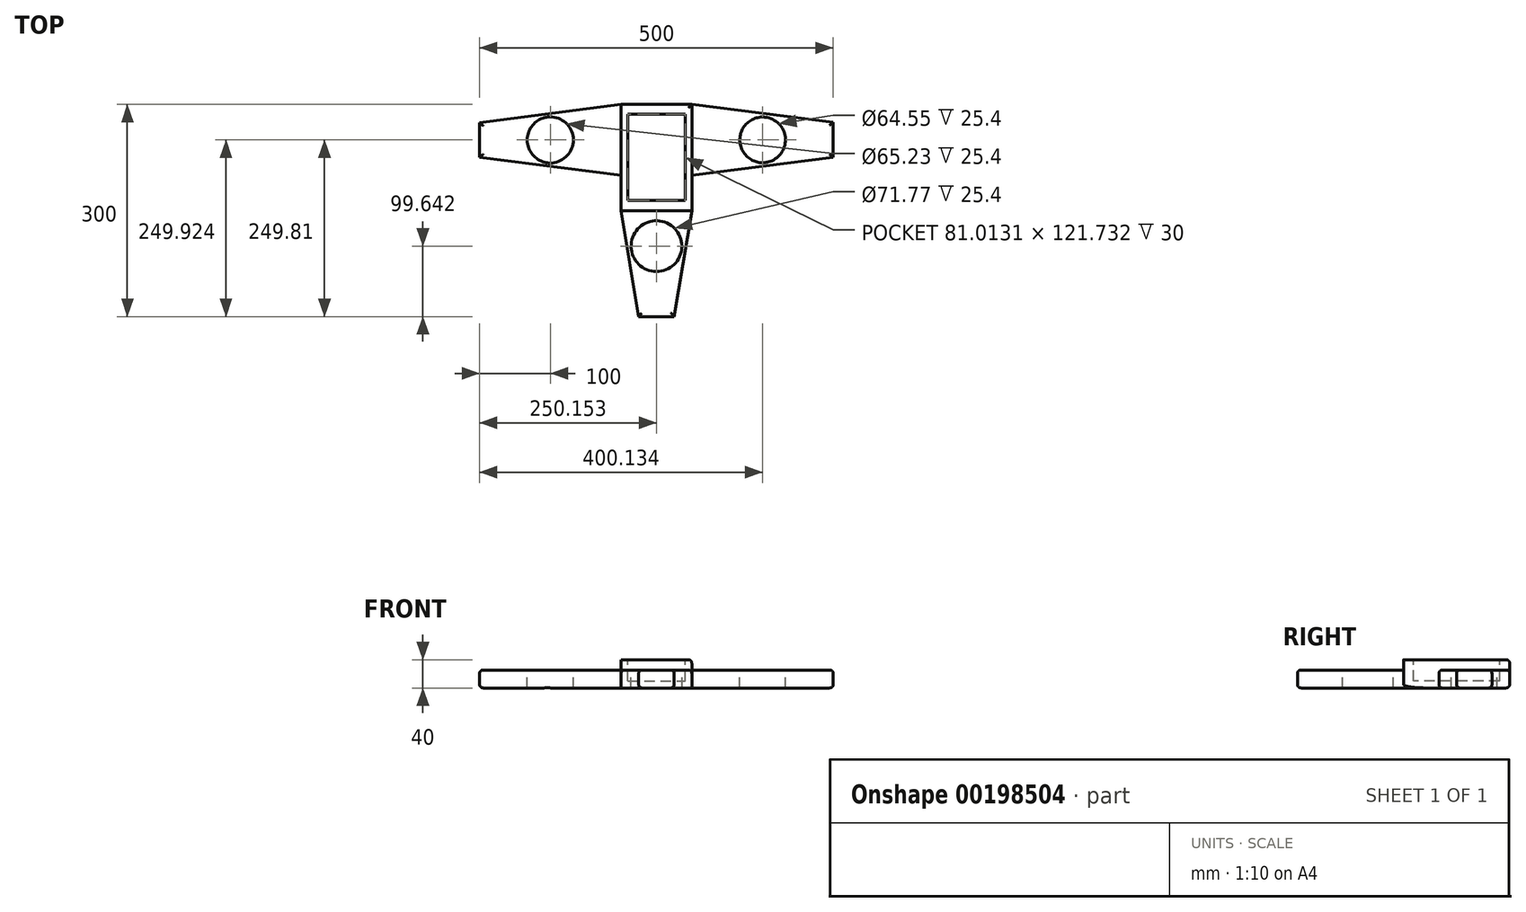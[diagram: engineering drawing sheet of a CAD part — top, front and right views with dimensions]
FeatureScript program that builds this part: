
annotation { "Feature Type Name" : "Feature", "Feature Type Description" : "" }
export const myFeature = defineFeature(function(context is Context, id is Id, definition is map)
    precondition{}
    {
        {
            var Q0;
            Q0=qCreatedBy(makeId("Top.planeOp"),FACE);
            var sketch = newSketch(context, id + "F0", { "sketchPlane" : qUnion([Q0])});
            skLineSegment(sketch, "E0.bottom", {"start": v(50, 50) * mm, "end": v(-50, 50) * mm});
            skLineSegment(sketch, "E0.top", {"start": v(50, -50) * mm, "end": v(-50, -50) * mm});
            skLineSegment(sketch, "E0.left", {"start": v(50, 50) * mm, "end": v(50, -50) * mm});
            skLineSegment(sketch, "E0.right", {"start": v(-50, 50) * mm, "end": v(-50, -50) * mm});
            skPoint(sketch, "E0.middle", {"position": v(0, 0) * mm});
            skLineSegment(sketch, "E1", {"start": v(-50, 25) * mm, "end": v(50, 25) * mm, "construction": true});
            skLineSegment(sketch, "E2", {"start": v(-50, -25) * mm, "end": v(50, -25) * mm, "construction": true});
            skLineSegment(sketch, "E3", {"start": v(-250, 24.24) * mm, "end": v(-45.96, 25) * mm, "construction": true});
            skLineSegment(sketch, "E4", {"start": v(-50, -25) * mm, "end": v(-250, -25) * mm, "construction": true});
            skLineSegment(sketch, "E5", {"start": v(50, 25) * mm, "end": v(250, 25) * mm, "construction": true});
            skLineSegment(sketch, "E6", {"start": v(50, -25) * mm, "end": v(250, -25) * mm, "construction": true});
            skLineSegment(sketch, "E7", {"start": v(-250, 24.24) * mm, "end": v(-50, 50) * mm});
            skLineSegment(sketch, "E8", {"start": v(-250, -25) * mm, "end": v(-50, -50) * mm});
            skLineSegment(sketch, "E9", {"start": v(-250, 24.24) * mm, "end": v(-250, -25) * mm});
            skLineSegment(sketch, "E10", {"start": v(50, 50) * mm, "end": v(250, 25) * mm});
            skLineSegment(sketch, "E11", {"start": v(50, -50) * mm, "end": v(250, -25) * mm});
            skLineSegment(sketch, "E12", {"start": v(250, 25) * mm, "end": v(250, -25) * mm});
            skLineSegment(sketch, "E13", {"start": v(-50, -50) * mm, "end": v(-50, -100) * mm});
            skLineSegment(sketch, "E14", {"start": v(-50, -100) * mm, "end": v(50, -100) * mm});
            skLineSegment(sketch, "E15", {"start": v(50, -100) * mm, "end": v(50, -50) * mm});
            skLineSegment(sketch, "E16", {"start": v(-25, -50) * mm, "end": v(-25, -100) * mm, "construction": true});
            skLineSegment(sketch, "E17", {"start": v(-25, -100) * mm, "end": v(25, -50) * mm, "construction": true});
            skLineSegment(sketch, "E18", {"start": v(25, -50) * mm, "end": v(25, -100) * mm, "construction": true});
            skLineSegment(sketch, "E19", {"start": v(-25, -100) * mm, "end": v(-25, -250) * mm, "construction": true});
            skLineSegment(sketch, "E20", {"start": v(25, -100) * mm, "end": v(25, -250) * mm, "construction": true});
            skLineSegment(sketch, "E21", {"start": v(-50, -100) * mm, "end": v(-25, -250) * mm});
            skLineSegment(sketch, "E22", {"start": v(25, -250) * mm, "end": v(50, -100) * mm});
            skLineSegment(sketch, "E23", {"start": v(-25, -250) * mm, "end": v(25, -250) * mm});
            skSolve(sketch);
        }
        {
            var Q0;
            Q0=makeQuery(id+"F0.imprint","IMPRINT",FACE,{"disambiguationData":[TD([[makeQuery(id+"F0.imprint","IMPRINT",EDGE,{"derivedFrom":sQuery(id+"F0.wireOp",EDGE,"E0.bottom")}),1.0]])]});
            extrude(context, id + "F1", {"entities" : qUnion([Q0]), "depth" : 40 * mm});
        }
        {
            var Q0;
            Q0=makeQuery(id+"F0.imprint","IMPRINT",FACE,{"disambiguationData":[TD([[makeQuery(id+"F0.imprint","IMPRINT",EDGE,{"derivedFrom":sQuery(id+"F0.wireOp",EDGE,"E0.left")}),1.0]])]});
            extrude(context, id + "F2", {"entities" : qUnion([Q0]), "operationType" : NewBodyOperationType.ADD, "depth" : 10 * mm});
        }
        {
            var Q0;
            Q0=makeQuery(id+"F0.imprint","IMPRINT",FACE,{"disambiguationData":[TD([[makeQuery(id+"F0.imprint","IMPRINT",EDGE,{"derivedFrom":sQuery(id+"F0.wireOp",EDGE,"E0.right")}),-1.0]])]});
            extrude(context, id + "F3", {"entities" : qUnion([Q0]), "operationType" : NewBodyOperationType.ADD, "depth" : 10 * mm});
        }
        {
            var Q0;
            Q0 = qSketchRegion(id + "F0", true);
            extrude(context, id + "F4", {"entities" : qUnion([Q0]), "operationType" : NewBodyOperationType.ADD, "depth" : 25.4 * mm});
        }
        {
            var Q0;
            Q0=makeQuery(id+"F0.imprint","IMPRINT",FACE,{"disambiguationData":[TD([[makeQuery(id+"F0.imprint","IMPRINT",EDGE,{"derivedFrom":sQuery(id+"F0.wireOp",EDGE,"E0.top")}),1.0]])]});
            extrude(context, id + "F5", {"entities" : qUnion([Q0]), "operationType" : NewBodyOperationType.ADD, "depth" : 40 * mm});
        }
        {
            var Q0;
            {var subQ0=sQuery(id+"F0.wireOp",EDGE,"E7");var subQ1=sQuery(id+"F0.wireOp",EDGE,"E13");var subQ2=sQuery(id+"F0.wireOp",EDGE,"E9");var subQ3=sQuery(id+"F0.wireOp",EDGE,"E8");var subQ4=sQuery(id+"F0.wireOp",EDGE,"E0.bottom");var subQ5=makeQuery(id+"F4.opExtrude","CAP_FACE",FACE,{"disambiguationData":[OSD([subQ4,subQ0,subQ3,subQ2,sQuery(id+"F0.wireOp",EDGE,"E10"),sQuery(id+"F0.wireOp",EDGE,"E11"),sQuery(id+"F0.wireOp",EDGE,"E12"),subQ1,sQuery(id+"F0.wireOp",EDGE,"E15"),sQuery(id+"F0.wireOp",EDGE,"E21"),sQuery(id+"F0.wireOp",EDGE,"E22"),sQuery(id+"F0.wireOp",EDGE,"E23")])],"isStart":false});Q0=makeQuery(id+"F4.boolean.opBoolean","SPLIT",FACE,{"disambiguationData":[TD([makeQuery(id+"F3.opExtrude","SWEPT_FACE",FACE,{"disambiguationData":[OSD([subQ0])]})])],"derivedFrom":subQ5});}
            var sketch = newSketch(context, id + "F6", { "sketchPlane" : qUnion([Q0])});
            skLineSegment(sketch, "E24", {"start": v(-250, -0.38) * mm, "end": v(250.13, 0) * mm, "construction": true});
            skLineSegment(sketch, "E25", {"start": v(0, 50.76) * mm, "end": v(0.23, -250.36) * mm, "construction": true});
            skLineSegment(sketch, "E26", {"start": v(-150, 37.12) * mm, "end": v(-150, -37.5) * mm, "construction": true});
            skLineSegment(sketch, "E27", {"start": v(150.1, 38.78) * mm, "end": v(150.17, -41) * mm, "construction": true});
            skLineSegment(sketch, "E28", {"start": v(-39.6, -150.39) * mm, "end": v(25.4, -150.34) * mm, "construction": true});
            skCircle(sketch, "E29", {"center": v(-150, -0.19) * mm, "radius": 32.61 * mm});
            skCircle(sketch, "E30", {"center": v(150.13, -0.08) * mm, "radius": 32.27 * mm});
            skCircle(sketch, "E31", {"center": v(0.15, -150.36) * mm, "radius": 35.89 * mm});
            skSolve(sketch);
        }
        {
            var Q0;
            Q0=makeQuery(id+"F6.imprint","IMPRINT",FACE,{"disambiguationData":[TD([[makeQuery(id+"F6.imprint","IMPRINT",EDGE,{"derivedFrom":sQuery(id+"F6.wireOp",EDGE,"E29")}),1.0]])]});
            var Q1;
            Q1=makeQuery(id+"F6.imprint","IMPRINT",FACE,{"disambiguationData":[TD([[makeQuery(id+"F6.imprint","IMPRINT",EDGE,{"derivedFrom":sQuery(id+"F6.wireOp",EDGE,"E31")}),1.0]])]});
            var Q2;
            Q2=makeQuery(id+"F6.imprint","IMPRINT",FACE,{"disambiguationData":[TD([[makeQuery(id+"F6.imprint","IMPRINT",EDGE,{"derivedFrom":sQuery(id+"F6.wireOp",EDGE,"E30")}),1.0]])]});
            extrude(context, id + "F7", {"entities" : qUnion([Q0, Q1, Q2]), "operationType" : NewBodyOperationType.REMOVE, "oppositeDirection" : true, "depth" : 51.3 * mm});
        }
        {
            var Q0;
            {var subQ0=sQuery(id+"F0.wireOp",EDGE,"E0.top");Q0=makeQuery(id+"F5.boolean.opBoolean","MERGE",FACE,{"derivedFrom":[makeQuery(id+"F1.opExtrude","CAP_FACE",FACE,{"disambiguationData":[OSD([sQuery(id+"F0.wireOp",EDGE,"E0.bottom"),subQ0,sQuery(id+"F0.wireOp",EDGE,"E0.left"),sQuery(id+"F0.wireOp",EDGE,"E0.right")])],"isStart":false}),makeQuery(id+"F5.opExtrude","CAP_FACE",FACE,{"disambiguationData":[OSD([subQ0,sQuery(id+"F0.wireOp",EDGE,"E13"),sQuery(id+"F0.wireOp",EDGE,"E14"),sQuery(id+"F0.wireOp",EDGE,"E15")])],"isStart":false})]});}
            var sketch = newSketch(context, id + "F8", { "sketchPlane" : qUnion([Q0])});
            skLineSegment(sketch, "E32", {"start": v(-50, 40) * mm, "end": v(50, 40) * mm, "construction": true});
            skLineSegment(sketch, "E33", {"start": v(40, 50) * mm, "end": v(40, -100) * mm, "construction": true});
            skLineSegment(sketch, "E34", {"start": v(-40, 50) * mm, "end": v(-40, -100) * mm, "construction": true});
            skLineSegment(sketch, "E35", {"start": v(-50, -90) * mm, "end": v(50, -90) * mm, "construction": true});
            skLineSegment(sketch, "E36", {"start": v(-40, 40) * mm, "end": v(40, 40) * mm});
            skLineSegment(sketch, "E37", {"start": v(40, 40) * mm, "end": v(40, -90) * mm});
            skLineSegment(sketch, "E38", {"start": v(40, -90) * mm, "end": v(-40, -90) * mm});
            skLineSegment(sketch, "E39", {"start": v(-40, -90) * mm, "end": v(-40, 40) * mm});
            skSolve(sketch);
        }
        {
            var Q0;
            Q0=makeQuery(id+"F8.imprint","IMPRINT",FACE,{"disambiguationData":[TD([[makeQuery(id+"F8.imprint","IMPRINT",EDGE,{"derivedFrom":sQuery(id+"F8.wireOp",EDGE,"E36")}),-1.0]])]});
            extrude(context, id + "F9", {"entities" : qUnion([Q0]), "operationType" : NewBodyOperationType.ADD, "oppositeDirection" : true, "depth" : 40 * mm});
        }
        {
            var Q0;
            {var subQ0=sQuery(id+"F0.wireOp",EDGE,"E0.top");Q0=makeQuery(id+"F5.boolean.opBoolean","MERGE",FACE,{"derivedFrom":[makeQuery(id+"F1.opExtrude","CAP_FACE",FACE,{"disambiguationData":[OSD([sQuery(id+"F0.wireOp",EDGE,"E0.bottom"),subQ0,sQuery(id+"F0.wireOp",EDGE,"E0.left"),sQuery(id+"F0.wireOp",EDGE,"E0.right")])],"isStart":false}),makeQuery(id+"F5.opExtrude","CAP_FACE",FACE,{"disambiguationData":[OSD([subQ0,sQuery(id+"F0.wireOp",EDGE,"E13"),sQuery(id+"F0.wireOp",EDGE,"E14"),sQuery(id+"F0.wireOp",EDGE,"E15")])],"isStart":false})]});}
            var sketch = newSketch(context, id + "F10", { "sketchPlane" : qUnion([Q0])});
            skLineSegment(sketch, "E40.bottom", {"start": v(-40.22, 36.05) * mm, "end": v(40.8, 36.05) * mm});
            skLineSegment(sketch, "E40.top", {"start": v(-40.22, -85.68) * mm, "end": v(40.8, -85.68) * mm});
            skLineSegment(sketch, "E40.left", {"start": v(-40.22, 36.05) * mm, "end": v(-40.22, -85.68) * mm});
            skLineSegment(sketch, "E40.right", {"start": v(40.8, 36.05) * mm, "end": v(40.8, -85.68) * mm});
            skSolve(sketch);
        }
        {
            var Q0;
            Q0=makeQuery(id+"F10.imprint","IMPRINT",FACE,{"disambiguationData":[TD([[makeQuery(id+"F10.imprint","IMPRINT",EDGE,{"derivedFrom":sQuery(id+"F10.wireOp",EDGE,"E40.bottom")}),-1.0]])]});
            extrude(context, id + "F11", {"entities" : qUnion([Q0]), "operationType" : NewBodyOperationType.REMOVE, "oppositeDirection" : true, "depth" : 30 * mm});
        }
        {
            var Q0;
            Q0=makeQuery(id+"F4.opExtrude","CAP_EDGE",EDGE,{"disambiguationData":[OSD([sQuery(id+"F0.wireOp",EDGE,"E10")])],"isStart":false});
            var Q1;
            Q1=makeQuery(id+"F4.opExtrude","CAP_EDGE",EDGE,{"disambiguationData":[OSD([sQuery(id+"F0.wireOp",EDGE,"E12")])],"isStart":false});
            var Q2;
            Q2=makeQuery(id+"F4.opExtrude","CAP_EDGE",EDGE,{"disambiguationData":[OSD([sQuery(id+"F0.wireOp",EDGE,"E11")])],"isStart":false});
            var Q3;
            Q3=makeQuery(id+"F5.boolean.opBoolean","MERGE",EDGE,{"derivedFrom":[makeQuery(id+"F1.opExtrude","CAP_EDGE",EDGE,{"disambiguationData":[OSD([sQuery(id+"F0.wireOp",EDGE,"E0.left")])],"isStart":false}),makeQuery(id+"F5.opExtrude","CAP_EDGE",EDGE,{"disambiguationData":[OSD([sQuery(id+"F0.wireOp",EDGE,"E15")])],"isStart":false})]});
            var Q4;
            Q4=makeQuery(id+"F11.boolean.opBoolean","COPY",EDGE,{"derivedFrom":makeQuery(id+"F11.opExtrude","CAP_EDGE",EDGE,{"disambiguationData":[OSD([sQuery(id+"F10.wireOp",EDGE,"E40.right")])],"isStart":true})});
            var Q5;
            Q5=makeQuery(id+"F11.boolean.opBoolean","COPY",EDGE,{"derivedFrom":makeQuery(id+"F11.opExtrude","CAP_EDGE",EDGE,{"disambiguationData":[OSD([sQuery(id+"F10.wireOp",EDGE,"E40.bottom")])],"isStart":true})});
            var Q6;
            Q6=makeQuery(id+"F11.boolean.opBoolean","COPY",EDGE,{"derivedFrom":makeQuery(id+"F11.opExtrude","CAP_EDGE",EDGE,{"disambiguationData":[OSD([sQuery(id+"F10.wireOp",EDGE,"E40.left")])],"isStart":true})});
            var Q7;
            Q7=makeQuery(id+"F11.boolean.opBoolean","COPY",EDGE,{"derivedFrom":makeQuery(id+"F11.opExtrude","CAP_EDGE",EDGE,{"disambiguationData":[OSD([sQuery(id+"F10.wireOp",EDGE,"E40.top")])],"isStart":true})});
            var Q8;
            Q8=makeQuery(id+"F1.opExtrude","CAP_EDGE",EDGE,{"disambiguationData":[OSD([sQuery(id+"F0.wireOp",EDGE,"E0.bottom")])],"isStart":false});
            var Q9;
            Q9=makeQuery(id+"F4.opExtrude","CAP_EDGE",EDGE,{"disambiguationData":[OSD([sQuery(id+"F0.wireOp",EDGE,"E7")])],"isStart":false});
            var Q10;
            Q10=makeQuery(id+"F4.opExtrude","CAP_EDGE",EDGE,{"disambiguationData":[OSD([sQuery(id+"F0.wireOp",EDGE,"E8")])],"isStart":false});
            var Q11;
            Q11=makeQuery(id+"F4.opExtrude","CAP_EDGE",EDGE,{"disambiguationData":[OSD([sQuery(id+"F0.wireOp",EDGE,"E9")])],"isStart":false});
            var Q12;
            Q12=makeQuery(id+"F4.opExtrude","CAP_EDGE",EDGE,{"disambiguationData":[OSD([sQuery(id+"F0.wireOp",EDGE,"E21")])],"isStart":false});
            var Q13;
            Q13=makeQuery(id+"F4.opExtrude","CAP_EDGE",EDGE,{"disambiguationData":[OSD([sQuery(id+"F0.wireOp",EDGE,"E23")])],"isStart":false});
            var Q14;
            Q14=makeQuery(id+"F4.opExtrude","CAP_EDGE",EDGE,{"disambiguationData":[OSD([sQuery(id+"F0.wireOp",EDGE,"E22")])],"isStart":false});
            var Q15;
            Q15=makeQuery(id+"F4.opExtrude","CAP_EDGE",EDGE,{"disambiguationData":[OSD([sQuery(id+"F0.wireOp",EDGE,"E23")])],"isStart":true});
            var Q16;
            Q16=makeQuery(id+"F4.opExtrude","CAP_EDGE",EDGE,{"disambiguationData":[OSD([sQuery(id+"F0.wireOp",EDGE,"E22")])],"isStart":true});
            var Q17;
            Q17=makeQuery(id+"F4.opExtrude","CAP_EDGE",EDGE,{"disambiguationData":[OSD([sQuery(id+"F0.wireOp",EDGE,"E21")])],"isStart":true});
            var Q18;
            Q18=makeQuery(id+"F3.opExtrude","CAP_EDGE",EDGE,{"disambiguationData":[OSD([sQuery(id+"F0.wireOp",EDGE,"E8")])],"isStart":true});
            var Q19;
            Q19=makeQuery(id+"F3.opExtrude","CAP_EDGE",EDGE,{"disambiguationData":[OSD([sQuery(id+"F0.wireOp",EDGE,"E9")])],"isStart":true});
            var Q20;
            Q20=makeQuery(id+"F3.opExtrude","CAP_EDGE",EDGE,{"disambiguationData":[OSD([sQuery(id+"F0.wireOp",EDGE,"E7")])],"isStart":true});
            var Q21;
            Q21=makeQuery(id+"F1.opExtrude","CAP_EDGE",EDGE,{"disambiguationData":[OSD([sQuery(id+"F0.wireOp",EDGE,"E0.bottom")])],"isStart":true});
            var Q22;
            Q22=makeQuery(id+"F2.opExtrude","CAP_EDGE",EDGE,{"disambiguationData":[OSD([sQuery(id+"F0.wireOp",EDGE,"E10")])],"isStart":true});
            var Q23;
            Q23=makeQuery(id+"F2.opExtrude","CAP_EDGE",EDGE,{"disambiguationData":[OSD([sQuery(id+"F0.wireOp",EDGE,"E12")])],"isStart":true});
            var Q24;
            Q24=makeQuery(id+"F2.opExtrude","CAP_EDGE",EDGE,{"disambiguationData":[OSD([sQuery(id+"F0.wireOp",EDGE,"E11")])],"isStart":true});
            fillet(context, id + "F12", {"entities" : qUnion([Q0, Q1, Q2, Q3, Q4, Q5, Q6, Q7, Q8, Q9, Q10, Q11, Q12, Q13, Q14, Q15, Q16, Q17, Q18, Q19, Q20, Q21, Q22, Q23, Q24]), "radius" : 5.08 * mm, "tangentPropagation" : true, "allowEdgeOverflow" : false});
        }
    });
